# Revit family: NBS_AndersonGECLtd_Splshbcks_StainlessSteelSplashback
name_source: partatom
category: Furniture
revit_build: Autodesk Revit 2017 (Build: 20160225_1515(x64)
units: mm (PartAtom-declared; Revit-internal decimal feet)

## family parameters
Cut with Voids When Loaded = No
Host = Face
Room Calculation Point = No
Shared = No

## types (1)
- StainlessSteelSplashback
    AssetType = Fixed
    BIMObjectName = NBS_AndersonGECLtd_Splashbacks_StainlessSteelSplashback
    Category = Pr_40_30_30_45:Kitchen splashbacks
    CodePerformance = EN 1.4301
    CornersOptions = Welded, unwelded
    Default Elevation = 900 mm  [stored 2.95276 ft]
    Description = Stainless steel panels and splashbacks
    DurationUnit = year
    Edges = Folded
    ExpectedLife = 30 years
    Features = Easy to clean
    Finish = Brushed satin
    FixingHoles = As required
    IfcExportAs = IfcFurnitureType
    IfcExportType = SPLASHBACK
    IsBuiltIn = Yes
    ManufacturerName = Anderson, GEC Ltd
    ManufacturerURL = www.gecanderson.co.uk
    Material = Stainless steel
    ModelReference = Stainless Steel Splashbacks
    NBSCertification = www.nationalbimlibrary.com/cert/uoaz4ilh
    NBSDescription = Splashbacks
    NBSReference = 45-35-15/464
    Name = Splashbacks_StainlessSteelSplashback_AndersonGECLtd
    NominalDepth = 20 mm  [stored 0.0656168 ft]
    NominalHeight = 1500 mm  [stored 4.92126 ft]
    NominalLength = 4000 mm  [stored 13.1234 ft]
    NominalWidth = 4000 mm  [stored 13.1234 ft]
    Options = Flat sheet available,, cut-outs for electrical points
    ProductInformation = http://www.gecanderson.co.uk
    Shape = Rectangle
    Size = 4000 x 1500 mm
    SplashbackHeight = 1500 mm  [stored 4.92126 ft]
    SplashbackMaterial = NBS_Concept
    SplashbackThickness = 20 mm  [stored 0.0656168 ft]
    SplashbackWidth = 4000 mm  [stored 13.1234 ft]
    Status = UNSET
    SustainabilityPerformance = 100% recyclable
    Thickness = 20 mm  [stored 0.0656168 ft]
    Uniclass2015Code = Pr_40_30_30_45
    Uniclass2015Title = Kitchen splashbacks
    Uniclass2015Version = Products v1.11
    Version = 1
    WarrantyDurationUnit = year

note: [stored X ft] marks values corroborated as IEEE doubles in the binary element streams (Revit-internal decimal feet)

## geometry (parser evidence)
native form markers: Sweep x3
no freeform markers — native parametric forms only
